# Revit family: 1013B
name_source: partatom
category: Plumbing Fixtures
revit_build: Autodesk Revit 2018 (Build: 20170223_1515(x64)
units: mm (PartAtom-declared; Revit-internal decimal feet)

## family parameters
Cut with Voids When Loaded = No
Host = Face
OmniClass Number = 23.45.05.14.14
OmniClass Title = Sinks/Lavatories
Part Type = Normal
Room Calculation Point = No
Round Connector Dimension = Use Diameter
Shared = Yes

## types (2) — shared parameters
Assembly Code = D2010400
CSSA - Hot & Cold Valve = No
CW Connection = Yes
CWFU = 1.5
Connection Size = 1 1/2"
Default Elevation = 34"
Description = Lavatory for Deck Mounted Valve, Enclosed Bottom
EG - Enviro-Glaze (for color selection see flier) = No
HW Connection = Yes
HWFU = 1.5
Height = 13 1/4"
Length = 18"
Manufacturer = Murdockmfg
Material = 14 gage, type 304 Stainless steel
Product Documentation Link = https://www.murdockmfg.com
Product URL = https://www.murdockmfg.com
SO2 - Cold Only Sensor Valve = No
STS - Cold Only Valve = No
SW - Wall Sleeve Wall Thickness = No
TF - 24V Transformer for Sensor Operated Valves = No
URL = https://www.murdockmfg.com
Vent Connection = No
WFU = 3
Warranty Documentation Link = https://www.murdockmfg.com
Waste Connection = Yes
Width = 18"

## per-type parameters (varying)
| type | 1013B-H1 - Lavatory Less Valve (Deck with 1 Hole) | 1013B-H34 - Lavatory Less Valve (Deck with 3 Holes, 4" centerset) | HCW Connection hole |
| 1013B-H1 | Yes | No | -1" |
| 1013B-H34 | No | Yes | 5" |

note: column(s) folded — value = type name in every type: Model

## geometry (parser evidence)
native form markers: Sweep x2
no freeform markers — native parametric forms only
